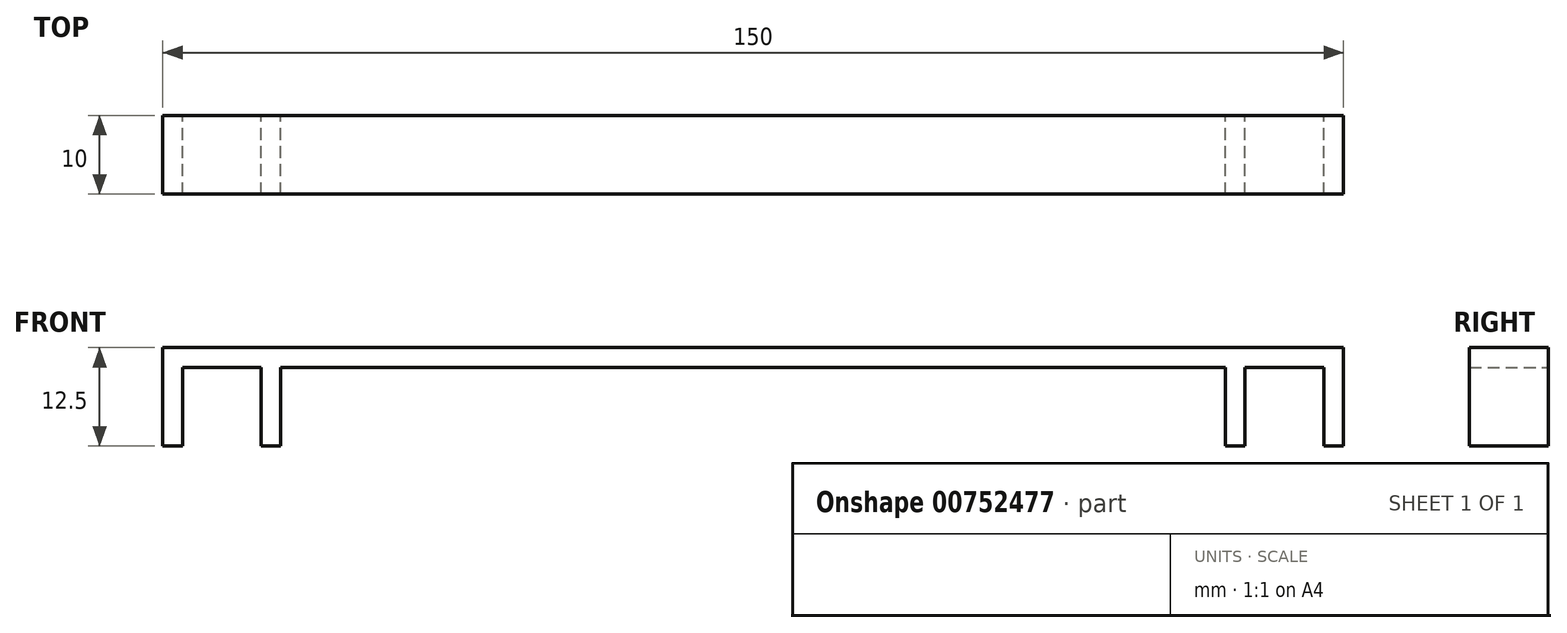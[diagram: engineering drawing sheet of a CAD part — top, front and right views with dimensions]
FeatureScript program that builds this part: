
annotation { "Feature Type Name" : "Feature", "Feature Type Description" : "" }
export const myFeature = defineFeature(function(context is Context, id is Id, definition is map)
    precondition{}
    {
        {
            var Q0;
            Q0=qCreatedBy(makeId("Front.planeOp"),FACE);
            var sketch = newSketch(context, id + "F0", { "sketchPlane" : qUnion([Q0])});
            skLineSegment(sketch, "E0.bottom", {"start": v(75, -1.25) * mm, "end": v(-75, -1.25) * mm});
            skLineSegment(sketch, "E0.top", {"start": v(75, 1.25) * mm, "end": v(-75, 1.25) * mm});
            skLineSegment(sketch, "E0.left", {"start": v(75, -1.25) * mm, "end": v(75, 1.25) * mm});
            skLineSegment(sketch, "E0.right", {"start": v(-75, -1.25) * mm, "end": v(-75, 1.25) * mm});
            skPoint(sketch, "E0.middle", {"position": v(0, 0) * mm});
            skSolve(sketch);
        }
        {
            var Q0;
            Q0=makeQuery(id+"F0.imprint","IMPRINT",FACE,{"disambiguationData":[TD([[makeQuery(id+"F0.imprint","IMPRINT",EDGE,{"derivedFrom":sQuery(id+"F0.wireOp",EDGE,"E0.bottom")}),-1.0]])]});
            extrude(context, id + "F1", {"entities" : qUnion([Q0]), "endBound" : BoundingType.SYMMETRIC, "depth" : 10 * mm, "offsetDistance" : 25 * mm});
        }
        {
            var Q0;
            Q0=makeQuery(id+"F1.opExtrude","SWEPT_FACE",FACE,{"disambiguationData":[OSD([sQuery(id+"F0.wireOp",EDGE,"E0.bottom")])]});
            var sketch = newSketch(context, id + "F2", { "sketchPlane" : qUnion([Q0])});
            skLineSegment(sketch, "E1", {"start": v(-72.5, 5) * mm, "end": v(-72.5, -5) * mm});
            skLineSegment(sketch, "E2", {"start": v(-62.5, 5) * mm, "end": v(-62.5, -5) * mm});
            skLineSegment(sketch, "E3", {"start": v(-60, 5) * mm, "end": v(-60, -5) * mm});
            skLineSegment(sketch, "E4.MirrorCS", {"start": v(60, 5) * mm, "end": v(60, -5) * mm});
            skLineSegment(sketch, "E5.MirrorCS", {"start": v(62.5, 5) * mm, "end": v(62.5, -5) * mm});
            skLineSegment(sketch, "E6.MirrorCS", {"start": v(72.5, 5) * mm, "end": v(72.5, -5) * mm});
            skSolve(sketch);
        }
        {
            var Q0;
            {var subQ0=sQuery(id+"F2.wireOp",EDGE,"E2");Q0=makeQuery(id+"F2.imprint","IMPRINT",FACE,{"disambiguationData":[TD([[makeQuery(id+"F2.imprint","IMPRINT",EDGE,{"derivedFrom":subQ0}),1.0]])]});}
            var Q1;
            {var subQ0=sQuery(id+"F2.wireOp",EDGE,"E1");Q1=makeQuery(id+"F2.imprint","IMPRINT",FACE,{"disambiguationData":[TD([[makeQuery(id+"F2.imprint","IMPRINT",EDGE,{"derivedFrom":subQ0}),-1.0]])]});}
            var Q2;
            {var subQ0=sQuery(id+"F2.wireOp",EDGE,"E4.MirrorCS");Q2=makeQuery(id+"F2.imprint","IMPRINT",FACE,{"disambiguationData":[TD([[makeQuery(id+"F2.imprint","IMPRINT",EDGE,{"derivedFrom":subQ0}),1.0]])]});}
            var Q3;
            {var subQ0=sQuery(id+"F2.wireOp",EDGE,"E6.MirrorCS");Q3=makeQuery(id+"F2.imprint","IMPRINT",FACE,{"disambiguationData":[TD([[makeQuery(id+"F2.imprint","IMPRINT",EDGE,{"derivedFrom":subQ0}),1.0]])]});}
            extrude(context, id + "F3", {"entities" : qUnion([Q0, Q1, Q2, Q3]), "operationType" : NewBodyOperationType.ADD, "depth" : 10 * mm, "offsetDistance" : 25 * mm});
        }
    });
